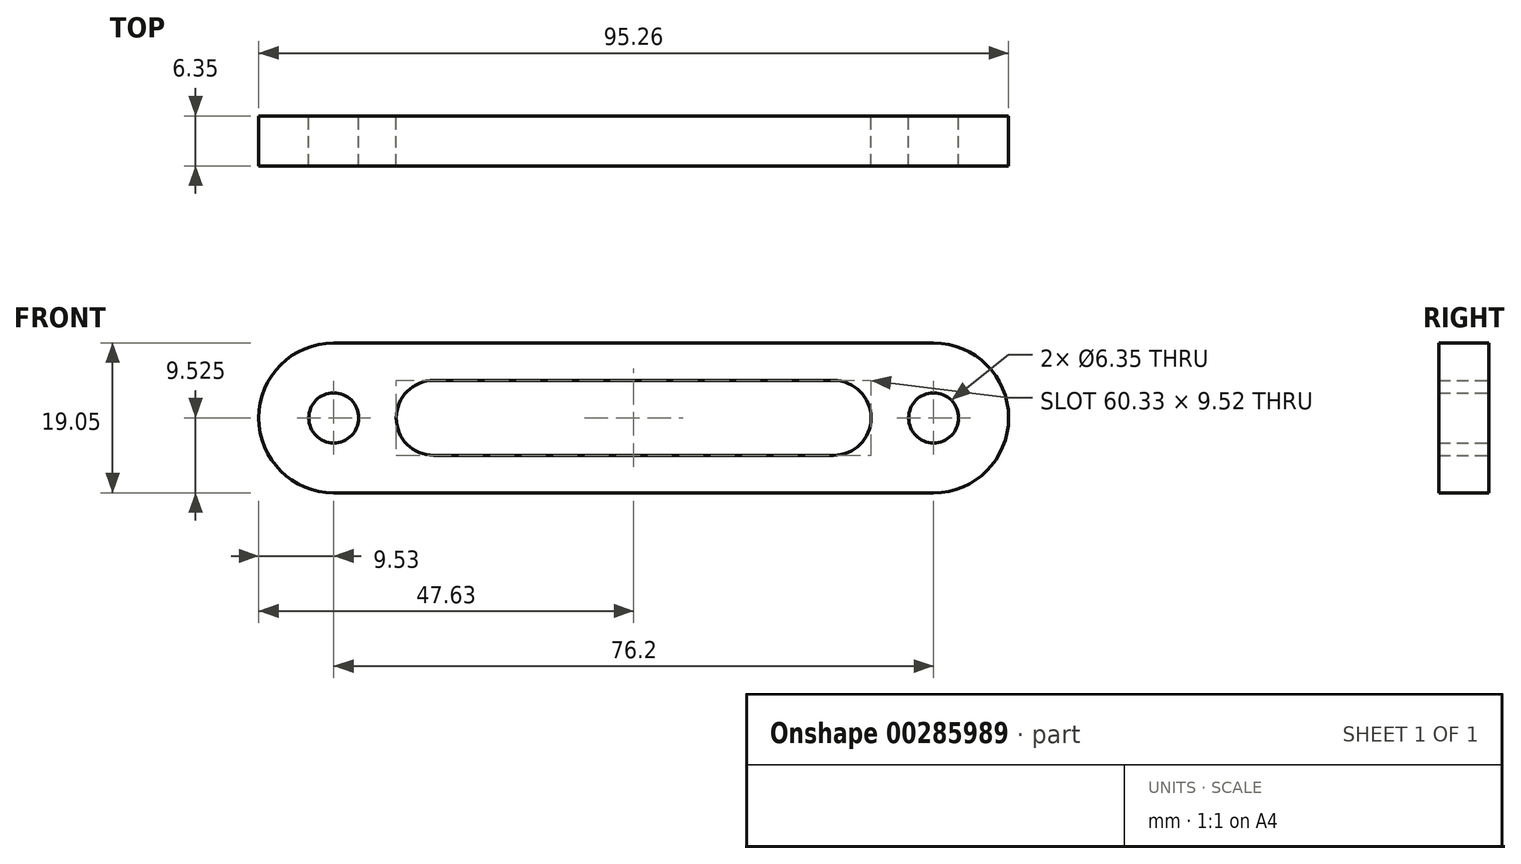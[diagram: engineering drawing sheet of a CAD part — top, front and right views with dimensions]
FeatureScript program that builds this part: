
annotation { "Feature Type Name" : "Feature", "Feature Type Description" : "" }
export const myFeature = defineFeature(function(context is Context, id is Id, definition is map)
    precondition{}
    {
        {
            var Q0;
            Q0=qCreatedBy(makeId("Front.planeOp"),FACE);
            var sketch = newSketch(context, id + "F0", { "sketchPlane" : qUnion([Q0])});
            skLineSegment(sketch, "E0.bottom", {"start": v(0, 0) * mm, "end": v(76.2, 0) * mm});
            skLineSegment(sketch, "E0.top", {"start": v(0, 19.05) * mm, "end": v(76.2, 19.05) * mm});
            skLineSegment(sketch, "E0.left", {"start": v(0, 0) * mm, "end": v(0, 19.05) * mm});
            skLineSegment(sketch, "E0.right", {"start": v(76.2, 0) * mm, "end": v(76.2, 19.05) * mm});
            skLineSegment(sketch, "E1.bottom", {"start": v(12.7, 14.29) * mm, "end": v(63.5, 14.29) * mm});
            skLineSegment(sketch, "E1.top", {"start": v(12.7, 4.76) * mm, "end": v(63.5, 4.76) * mm});
            skLineSegment(sketch, "E1.left", {"start": v(12.7, 14.29) * mm, "end": v(12.7, 4.76) * mm});
            skLineSegment(sketch, "E1.right", {"start": v(63.5, 14.29) * mm, "end": v(63.5, 4.76) * mm});
            skArc(sketch, "E2", {"start": v(63.5, 14.29) * mm, "mid": v(68.26, 9.53) * mm, "end": v(63.5, 4.76) * mm});
            skArc(sketch, "E3", {"start": v(12.7, 14.29) * mm, "mid": v(7.94, 9.53) * mm, "end": v(12.7, 4.76) * mm});
            skArc(sketch, "E4", {"start": v(76.2, 19.05) * mm, "mid": v(85.73, 9.53) * mm, "end": v(76.2, 0) * mm});
            skArc(sketch, "E5", {"start": v(0, 19.05) * mm, "mid": v(-9.53, 9.53) * mm, "end": v(0, 0) * mm});
            skCircle(sketch, "E6", {"center": v(0, 9.53) * mm, "radius": 3.18 * mm});
            skCircle(sketch, "E7", {"center": v(76.2, 9.53) * mm, "radius": 3.18 * mm});
            skSolve(sketch);
        }
        {
            var Q0;
            Q0 = qSketchRegion(id + "F0", true);
            extrude(context, id + "F1", {"entities" : qUnion([Q0]), "depth" : 6.35 * mm});
        }
    });
